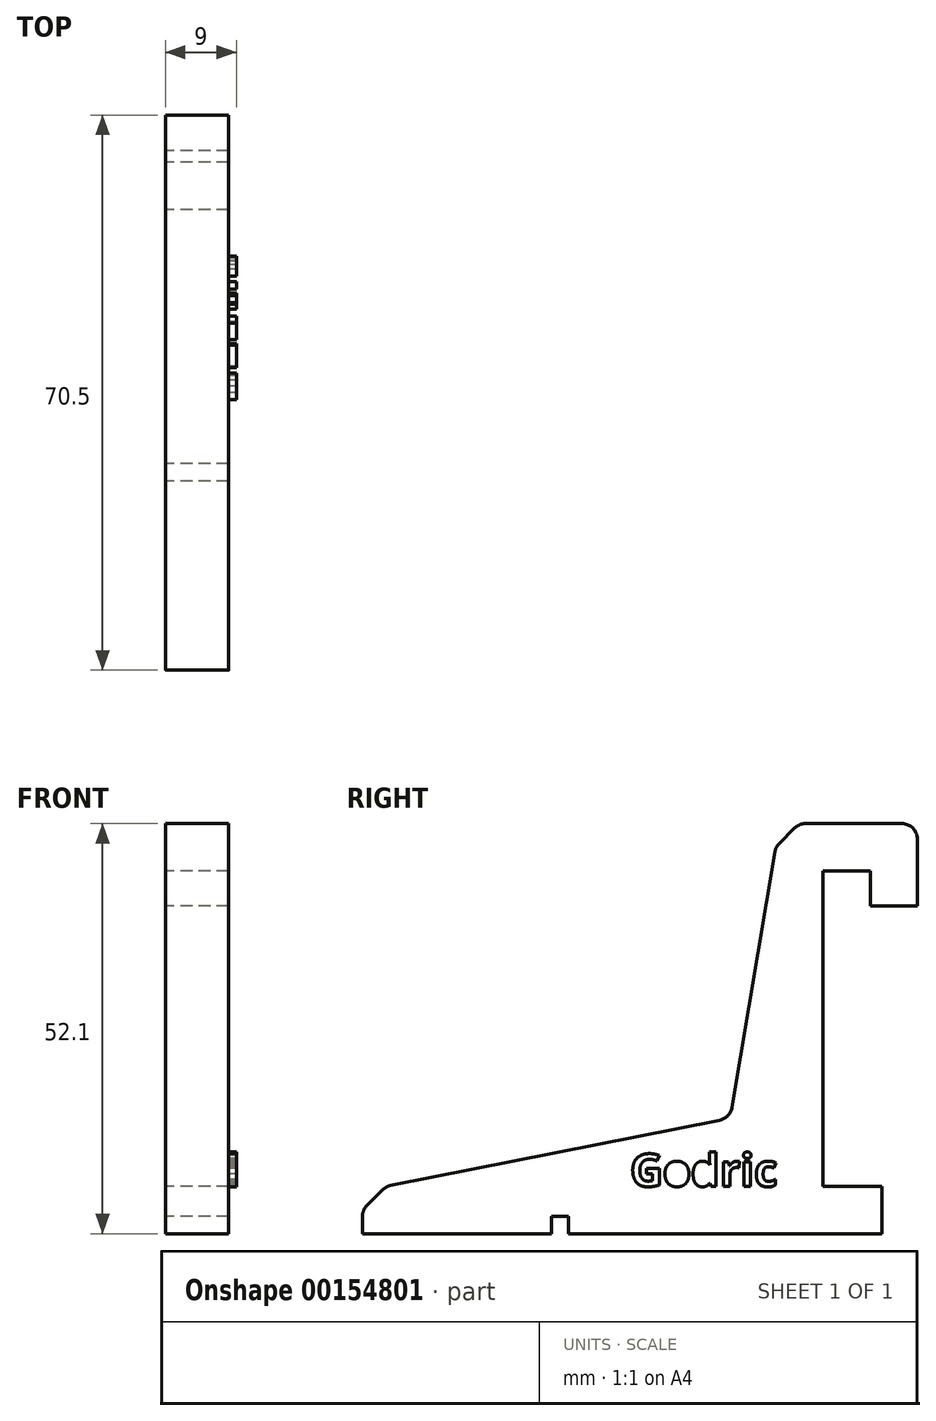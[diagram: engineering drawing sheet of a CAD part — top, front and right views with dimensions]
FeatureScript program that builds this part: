
annotation { "Feature Type Name" : "Feature", "Feature Type Description" : "" }
export const myFeature = defineFeature(function(context is Context, id is Id, definition is map)
    precondition{}
    {
        {
            var Q0;
            Q0=qCreatedBy(makeId("Right.planeOp"),FACE);
            var sketch = newSketch(context, id + "F0", { "sketchPlane" : qUnion([Q0])});
            skLineSegment(sketch, "E0.bottom", {"start": v(0, 0) * mm, "end": v(6, 0) * mm});
            skLineSegment(sketch, "E0.top", {"start": v(0, -40.1) * mm, "end": v(6, -40.1) * mm});
            skLineSegment(sketch, "E0.right", {"start": v(6, 0) * mm, "end": v(6, -3.5) * mm});
            skLineSegment(sketch, "E1.0", {"start": v(12, 6) * mm, "end": v(12, -3.5) * mm});
            skLineSegment(sketch, "E1.1", {"start": v(-3, 6) * mm, "end": v(12, 6) * mm});
            skLineSegment(sketch, "E2.0", {"start": v(7, -4.5) * mm, "end": v(11, -4.5) * mm});
            skLineSegment(sketch, "E3.0", {"start": v(7.5, -40.1) * mm, "end": v(7.5, -46.1) * mm});
            skLineSegment(sketch, "E4", {"start": v(7.5, -40.1) * mm, "end": v(6, -40.1) * mm});
            skLineSegment(sketch, "E5", {"start": v(0, 0) * mm, "end": v(0, -40.1) * mm});
            skPoint(sketch, "E6.visualSharp", {"position": v(6, -4.5) * mm});
            skPoint(sketch, "E7.visualSharp", {"position": v(12, -4.5) * mm});
            skLineSegment(sketch, "E8", {"start": v(-6, 3) * mm, "end": v(-3, 6) * mm});
            skLineSegment(sketch, "E9", {"start": v(7, -4.5) * mm, "end": v(6, -4.5) * mm});
            skLineSegment(sketch, "E10", {"start": v(6, -3.5) * mm, "end": v(6, -4.5) * mm});
            skLineSegment(sketch, "E11", {"start": v(12, -3.5) * mm, "end": v(12, -4.5) * mm});
            skLineSegment(sketch, "E12", {"start": v(11, -4.5) * mm, "end": v(12, -4.5) * mm});
            skLineSegment(sketch, "E13", {"start": v(7.5, -46.1) * mm, "end": v(-32.3, -46.1) * mm});
            skLineSegment(sketch, "E14", {"start": v(-58.5, -46.1) * mm, "end": v(-58.5, -43.1) * mm});
            skLineSegment(sketch, "E15.0", {"start": v(7.5, -40.1) * mm, "end": v(0, -40.1) * mm});
            skLineSegment(sketch, "E16", {"start": v(-58.5, -43.1) * mm, "end": v(-55.5, -40.1) * mm});
            skLineSegment(sketch, "E17", {"start": v(-55.5, -40.1) * mm, "end": v(-11.77, -31.41) * mm});
            skLineSegment(sketch, "E18", {"start": v(-6, 3) * mm, "end": v(-11.77, -31.41) * mm});
            skText(sketch, "E19", { "text": "Godric", "fontName": "OpenSans-Bold.ttf"});
            skLineSegment(sketch, "E20.trimOffspring", {"start": v(-39.6, -46.1) * mm, "end": v(-58.5, -46.1) * mm});
            skLineSegment(sketch, "E21", {"start": v(-39.6, -46.1) * mm, "end": v(-37.4, -46.1) * mm});
            skLineSegment(sketch, "E22.0", {"start": v(-34.5, -46.1) * mm, "end": v(-34.5, -43.9) * mm});
            skLineSegment(sketch, "E23.0", {"start": v(-32.3, -46.1) * mm, "end": v(-32.3, -43.9) * mm});
            skLineSegment(sketch, "E24.0", {"start": v(-32.3, -43.9) * mm, "end": v(-34.5, -43.9) * mm});
            skLineSegment(sketch, "E25.trimOffspring", {"start": v(-34.5, -46.1) * mm, "end": v(-37.4, -46.1) * mm});
            const initialGuessF0  = {"E19": [-0.0245, -0.0401, 1, 0, 0.00415]};
            skSetInitialGuess(sketch, initialGuessF0);
            skSolve(sketch);
        }
        {
            var Q0;
            Q0=makeQuery(id+"F0.imprint","IMPRINT",FACE,{"disambiguationData":[TD([[makeQuery(id+"F0.imprint","IMPRINT",EDGE,{"derivedFrom":sQuery(id+"F0.wireOp",EDGE,"E0.bottom")}),1.0]])]});
            extrude(context, id + "F1", {"entities" : qUnion([Q0]), "depth" : 8 * mm});
        }
        {
            var Q0;
            Q0=makeQuery(id+"F0.imprint","IMPRINT",FACE,{"disambiguationData":[TD([[makeQuery(id+"F0.imprint","IMPRINT",EDGE,{"derivedFrom":sQuery(id+"F0.wireOp",EDGE,"E19.sketch_text.stroke-19")}),1.0]])]});
            var Q1;
            Q1=makeQuery(id+"F0.imprint","IMPRINT",FACE,{"disambiguationData":[TD([[makeQuery(id+"F0.imprint","IMPRINT",EDGE,{"derivedFrom":sQuery(id+"F0.wireOp",EDGE,"E19.sketch_text.stroke-19")}),-1.0]])]});
            var Q2;
            Q2=makeQuery(id+"F0.imprint","IMPRINT",FACE,{"disambiguationData":[TD([[makeQuery(id+"F0.imprint","IMPRINT",EDGE,{"derivedFrom":sQuery(id+"F0.wireOp",EDGE,"E19.sketch_text.stroke-0")}),-1.0]])]});
            var Q3;
            Q3=makeQuery(id+"F0.imprint","IMPRINT",FACE,{"disambiguationData":[TD([[makeQuery(id+"F0.imprint","IMPRINT",EDGE,{"derivedFrom":sQuery(id+"F0.wireOp",EDGE,"E19.sketch_text.stroke-37")}),-1.0]])]});
            var Q4;
            Q4=makeQuery(id+"F0.imprint","IMPRINT",FACE,{"disambiguationData":[TD([[makeQuery(id+"F0.imprint","IMPRINT",EDGE,{"derivedFrom":sQuery(id+"F0.wireOp",EDGE,"E19.sketch_text.stroke-51")}),1.0]])]});
            var Q5;
            Q5=makeQuery(id+"F0.imprint","IMPRINT",FACE,{"disambiguationData":[TD([[makeQuery(id+"F0.imprint","IMPRINT",EDGE,{"derivedFrom":sQuery(id+"F0.wireOp",EDGE,"E19.sketch_text.stroke-60")}),-1.0]])]});
            var Q6;
            Q6=makeQuery(id+"F0.imprint","IMPRINT",FACE,{"disambiguationData":[TD([[makeQuery(id+"F0.imprint","IMPRINT",EDGE,{"derivedFrom":sQuery(id+"F0.wireOp",EDGE,"E19.sketch_text.stroke-73")}),-1.0]])]});
            var Q7;
            Q7=makeQuery(id+"F0.imprint","IMPRINT",FACE,{"disambiguationData":[TD([[makeQuery(id+"F0.imprint","IMPRINT",EDGE,{"derivedFrom":sQuery(id+"F0.wireOp",EDGE,"E19.sketch_text.stroke-78")}),-1.0]])]});
            var Q8;
            Q8=makeQuery(id+"F0.imprint","IMPRINT",FACE,{"disambiguationData":[TD([[makeQuery(id+"F0.imprint","IMPRINT",EDGE,{"derivedFrom":sQuery(id+"F0.wireOp",EDGE,"E19.sketch_text.stroke-82")}),-1.0]])]});
            extrude(context, id + "F2", {"entities" : qUnion([Q0, Q1, Q2, Q3, Q4, Q5, Q6, Q7, Q8]), "operationType" : NewBodyOperationType.ADD, "depth" : 9 * mm});
        }
        {
            var Q0;
            Q0=makeQuery(id+"F1.opExtrude","SWEPT_EDGE",EDGE,{"disambiguationData":[OSD([sQuery(id+"F0.wireOp",EDGE,"E14"),sQuery(id+"F0.wireOp",EDGE,"E16")])]});
            var Q1;
            Q1=makeQuery(id+"F1.opExtrude","SWEPT_EDGE",EDGE,{"disambiguationData":[OSD([sQuery(id+"F0.wireOp",EDGE,"E16"),sQuery(id+"F0.wireOp",EDGE,"E17")])]});
            var Q2;
            Q2=makeQuery(id+"F1.opExtrude","SWEPT_EDGE",EDGE,{"disambiguationData":[OSD([sQuery(id+"F0.wireOp",EDGE,"E17"),sQuery(id+"F0.wireOp",EDGE,"E18")])]});
            var Q3;
            Q3=makeQuery(id+"F1.opExtrude","SWEPT_EDGE",EDGE,{"disambiguationData":[OSD([sQuery(id+"F0.wireOp",EDGE,"E8"),sQuery(id+"F0.wireOp",EDGE,"E18")])]});
            var Q4;
            Q4=makeQuery(id+"F1.opExtrude","SWEPT_EDGE",EDGE,{"disambiguationData":[OSD([sQuery(id+"F0.wireOp",EDGE,"E1.1"),sQuery(id+"F0.wireOp",EDGE,"E8")])]});
            var Q5;
            Q5=makeQuery(id+"F1.opExtrude","SWEPT_EDGE",EDGE,{"disambiguationData":[OSD([sQuery(id+"F0.wireOp",EDGE,"E1.0"),sQuery(id+"F0.wireOp",EDGE,"E1.1")])]});
            fillet(context, id + "F3", {"entities" : qUnion([Q0, Q1, Q2, Q3, Q4, Q5]), "radius" : 2 * mm, "tangentPropagation" : true, "allowEdgeOverflow" : false});
        }
    });
